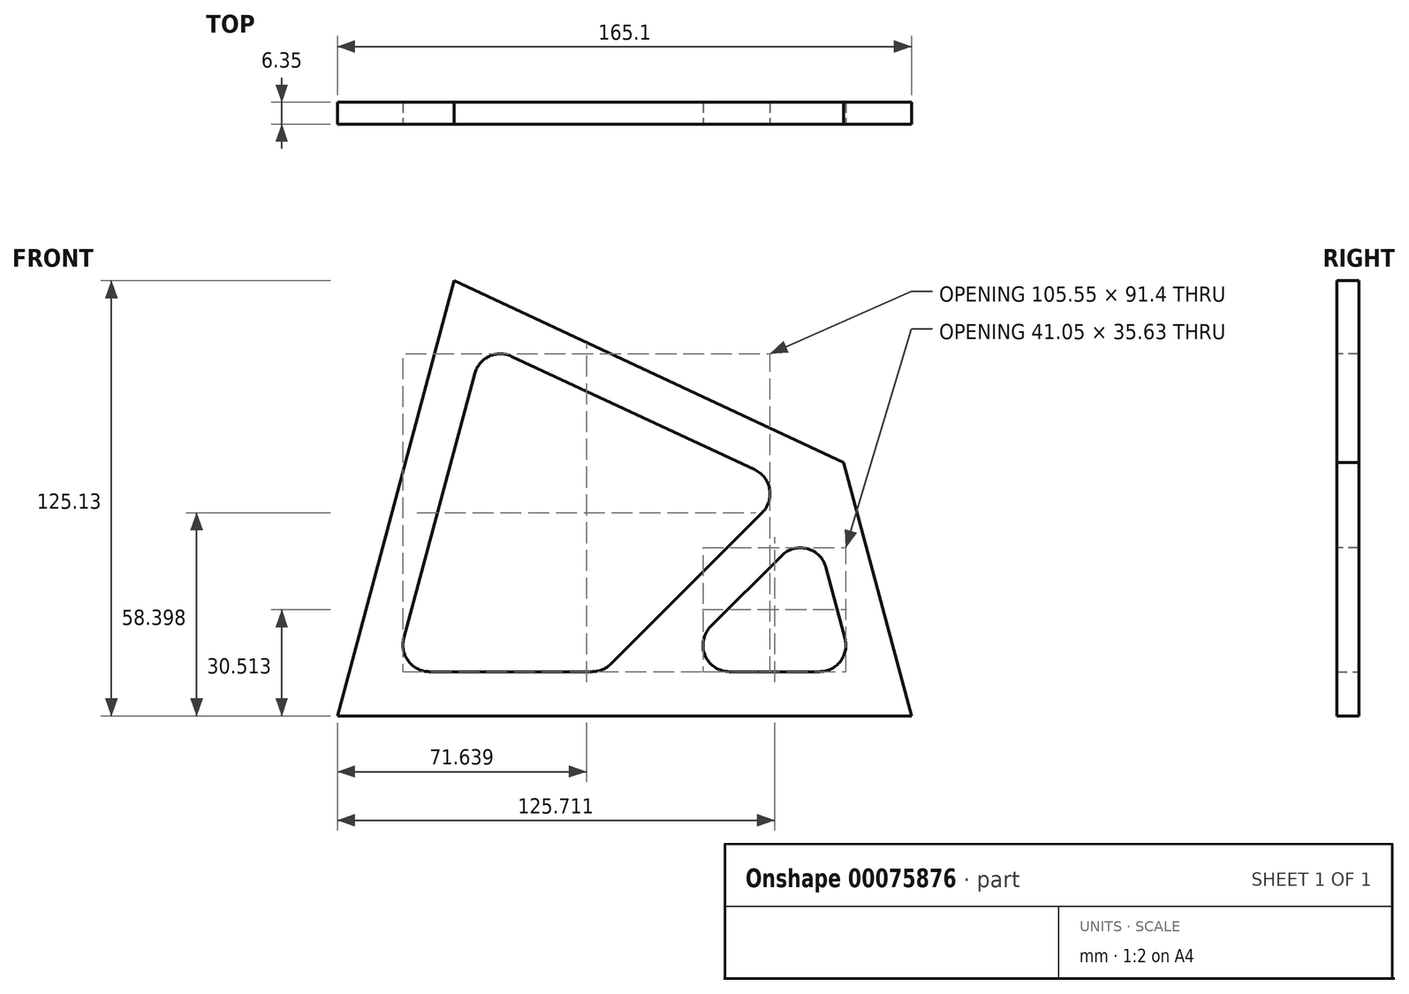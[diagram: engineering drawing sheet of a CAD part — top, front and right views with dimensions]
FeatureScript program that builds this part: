
annotation { "Feature Type Name" : "Feature", "Feature Type Description" : "" }
export const myFeature = defineFeature(function(context is Context, id is Id, definition is map)
    precondition{}
    {
        {
            var Q0;
            Q0=qCreatedBy(makeId("Front.planeOp"),FACE);
            var sketch = newSketch(context, id + "F0", { "sketchPlane" : qUnion([Q0])});
            skLineSegment(sketch, "E0", {"start": v(0, 0) * mm, "end": v(33.53, 125.13) * mm});
            skLineSegment(sketch, "E1", {"start": v(33.53, 125.13) * mm, "end": v(145.57, 72.88) * mm});
            skLineSegment(sketch, "E2", {"start": v(145.57, 72.88) * mm, "end": v(165.1, 0) * mm});
            skLineSegment(sketch, "E3", {"start": v(165.1, 0) * mm, "end": v(0, 0) * mm});
            skLineSegment(sketch, "E4", {"start": v(41.88, 107.22) * mm, "end": v(16.55, 12.7) * mm});
            skLineSegment(sketch, "E5", {"start": v(16.55, 12.7) * mm, "end": v(76.41, 12.7) * mm});
            skLineSegment(sketch, "E6", {"start": v(76.41, 12.7) * mm, "end": v(129.9, 66.18) * mm});
            skLineSegment(sketch, "E7", {"start": v(129.9, 66.18) * mm, "end": v(41.88, 107.22) * mm});
            skLineSegment(sketch, "E8", {"start": v(137.1, 55.43) * mm, "end": v(94.37, 12.7) * mm});
            skLineSegment(sketch, "E9", {"start": v(94.37, 12.7) * mm, "end": v(148.55, 12.7) * mm});
            skLineSegment(sketch, "E10", {"start": v(148.55, 12.7) * mm, "end": v(137.1, 55.43) * mm});
            skLineSegment(sketch, "E11", {"start": v(145.57, 72.88) * mm, "end": v(72.7, 0) * mm, "construction": true});
            skLineSegment(sketch, "E12", {"start": v(33.53, 125.13) * mm, "end": v(130.46, 125.13) * mm, "construction": true});
            skSolve(sketch);
        }
        {
            var Q0;
            Q0=makeQuery(id+"F0.imprint","IMPRINT",FACE,{"disambiguationData":[TD([[makeQuery(id+"F0.imprint","IMPRINT",EDGE,{"derivedFrom":sQuery(id+"F0.wireOp",EDGE,"E0")}),-1.0]])]});
            extrude(context, id + "F1", {"entities" : qUnion([Q0]), "depth" : 6.35 * mm});
        }
        {
            var Q0;
            Q0=makeQuery(id+"F1.opExtrude","SWEPT_EDGE",EDGE,{"disambiguationData":[OSD([sQuery(id+"F0.wireOp",EDGE,"E4"),sQuery(id+"F0.wireOp",EDGE,"E7")])]});
            var Q1;
            Q1=makeQuery(id+"F1.opExtrude","SWEPT_EDGE",EDGE,{"disambiguationData":[OSD([sQuery(id+"F0.wireOp",EDGE,"E4"),sQuery(id+"F0.wireOp",EDGE,"E5")])]});
            var Q2;
            Q2=makeQuery(id+"F1.opExtrude","SWEPT_EDGE",EDGE,{"disambiguationData":[OSD([sQuery(id+"F0.wireOp",EDGE,"E5"),sQuery(id+"F0.wireOp",EDGE,"E6")])]});
            var Q3;
            Q3=makeQuery(id+"F1.opExtrude","SWEPT_EDGE",EDGE,{"disambiguationData":[OSD([sQuery(id+"F0.wireOp",EDGE,"E6"),sQuery(id+"F0.wireOp",EDGE,"E7")])]});
            var Q4;
            Q4=makeQuery(id+"F1.opExtrude","SWEPT_EDGE",EDGE,{"disambiguationData":[OSD([sQuery(id+"F0.wireOp",EDGE,"E8"),sQuery(id+"F0.wireOp",EDGE,"E10")])]});
            var Q5;
            Q5=makeQuery(id+"F1.opExtrude","SWEPT_EDGE",EDGE,{"disambiguationData":[OSD([sQuery(id+"F0.wireOp",EDGE,"E8"),sQuery(id+"F0.wireOp",EDGE,"E9")])]});
            var Q6;
            Q6=makeQuery(id+"F1.opExtrude","SWEPT_EDGE",EDGE,{"disambiguationData":[OSD([sQuery(id+"F0.wireOp",EDGE,"E9"),sQuery(id+"F0.wireOp",EDGE,"E10")])]});
            fillet(context, id + "F2", {"entities" : qUnion([Q0, Q1, Q2, Q3, Q4, Q5, Q6]), "radius" : 7.62 * mm, "tangentPropagation" : true, "allowEdgeOverflow" : false});
        }
    });
